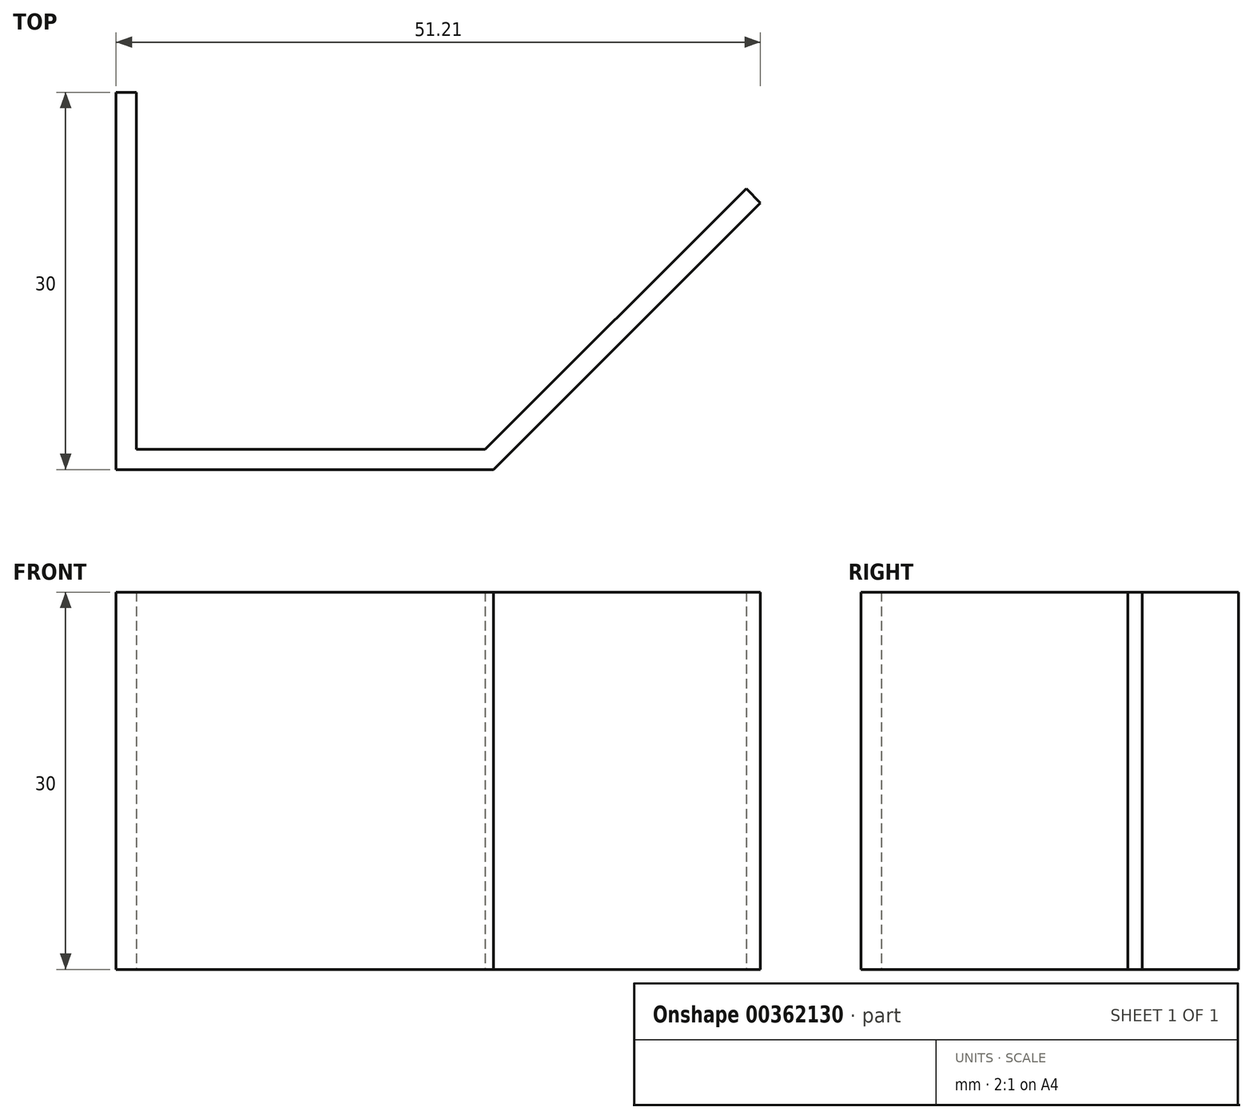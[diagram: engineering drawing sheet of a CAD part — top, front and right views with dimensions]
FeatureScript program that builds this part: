
annotation { "Feature Type Name" : "Feature", "Feature Type Description" : "" }
export const myFeature = defineFeature(function(context is Context, id is Id, definition is map)
    precondition{}
    {
        {
            var Q0;
            Q0=qCreatedBy(makeId("Top.planeOp"),FACE);
            var sketch = newSketch(context, id + "F0", { "sketchPlane" : qUnion([Q0])});
            skLineSegment(sketch, "E0", {"start": v(0, 30) * mm, "end": v(0, 0) * mm});
            skLineSegment(sketch, "E1", {"start": v(0, 0) * mm, "end": v(30, 0) * mm});
            skLineSegment(sketch, "E2", {"start": v(30, 0) * mm, "end": v(51.21, 21.21) * mm});
            skLineSegment(sketch, "E3", {"start": v(51.21, 21.21) * mm, "end": v(50.08, 22.34) * mm});
            skLineSegment(sketch, "E4", {"start": v(50.08, 22.34) * mm, "end": v(29.34, 1.6) * mm});
            skLineSegment(sketch, "E5", {"start": v(29.34, 1.6) * mm, "end": v(1.6, 1.6) * mm});
            skLineSegment(sketch, "E6", {"start": v(1.6, 1.6) * mm, "end": v(1.6, 30) * mm});
            skLineSegment(sketch, "E7", {"start": v(1.6, 30) * mm, "end": v(0, 30) * mm});
            skSolve(sketch);
        }
        {
            var Q0;
            Q0=makeQuery(id+"F0.imprint","IMPRINT",FACE,{"disambiguationData":[TD([[makeQuery(id+"F0.imprint","IMPRINT",EDGE,{"derivedFrom":sQuery(id+"F0.wireOp",EDGE,"E0")}),1.0]])]});
            extrude(context, id + "F1", {"entities" : qUnion([Q0]), "depth" : 30 * mm, "offsetDistance" : 25 * mm});
        }
    });
